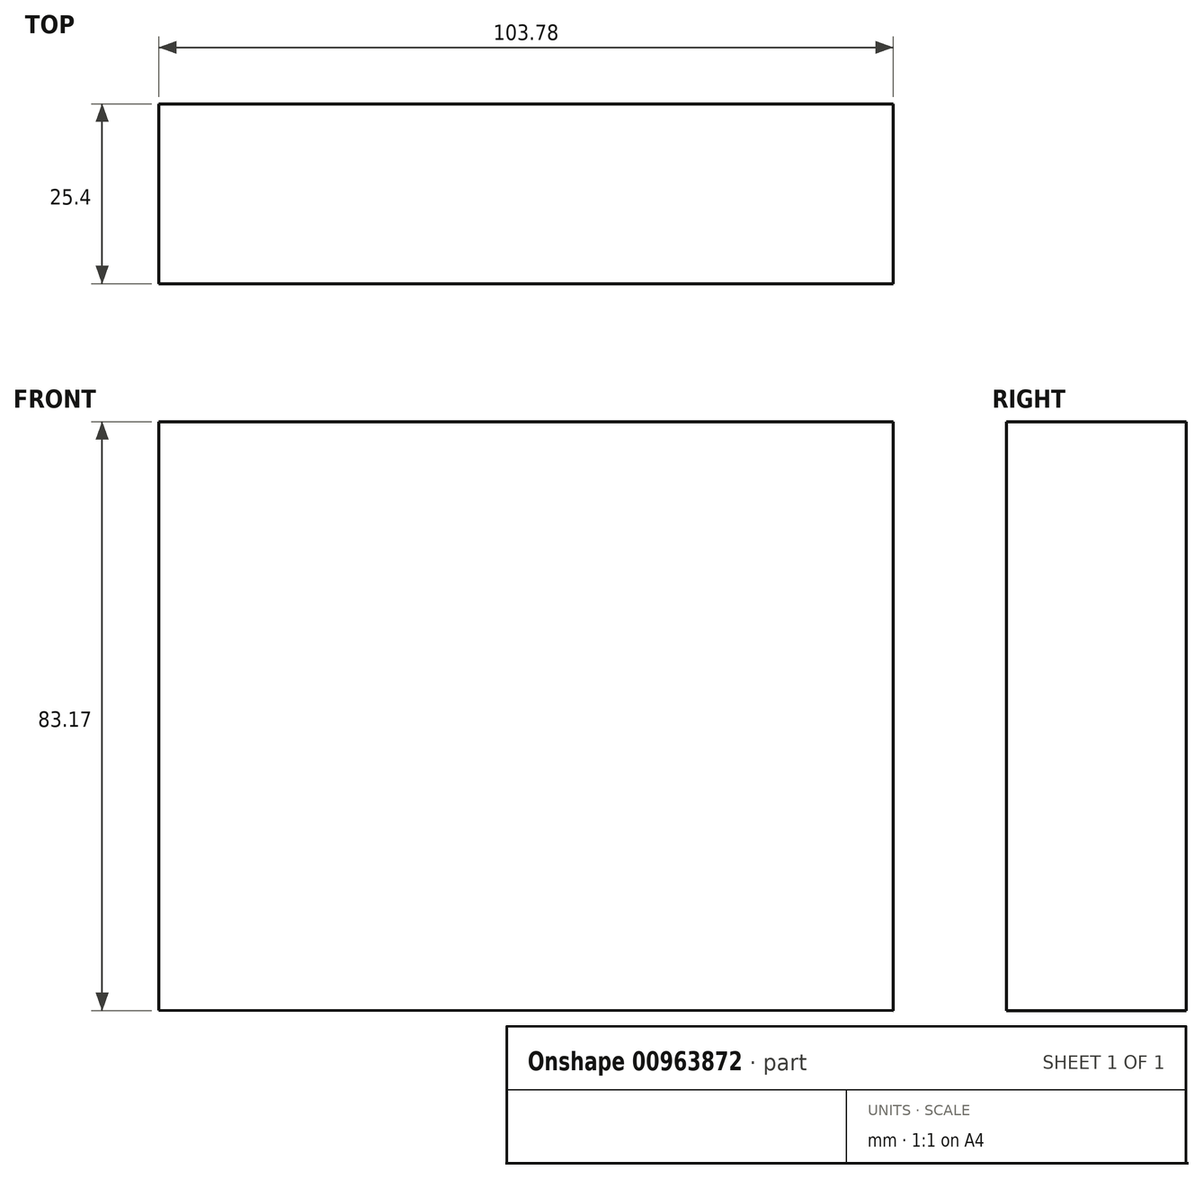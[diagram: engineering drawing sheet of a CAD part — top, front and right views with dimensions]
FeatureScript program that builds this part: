
annotation { "Feature Type Name" : "Feature", "Feature Type Description" : "" }
export const myFeature = defineFeature(function(context is Context, id is Id, definition is map)
    precondition{}
    {
        {
            var Q0;
            Q0=qCreatedBy(makeId("Front.planeOp"),FACE);
            var sketch = newSketch(context, id + "F0", { "sketchPlane" : qUnion([Q0])});
            skLineSegment(sketch, "E0", {"start": v(-44.93, 44.37) * mm, "end": v(58.85, 44.37) * mm});
            skLineSegment(sketch, "E1", {"start": v(58.85, 44.37) * mm, "end": v(58.85, -38.8) * mm});
            skLineSegment(sketch, "E2", {"start": v(58.85, -38.8) * mm, "end": v(-44.93, -38.74) * mm});
            skLineSegment(sketch, "E3", {"start": v(-44.93, 44.37) * mm, "end": v(-44.93, -38.74) * mm});
            skSolve(sketch);
        }
        {
            var Q0;
            Q0=makeQuery(id+"F0.imprint","IMPRINT",FACE,{"disambiguationData":[TD([[makeQuery(id+"F0.imprint","IMPRINT",EDGE,{"derivedFrom":sQuery(id+"F0.wireOp",EDGE,"E0")}),-1.0]])]});
            extrude(context, id + "F1", {"entities" : qUnion([Q0]), "endBound" : BoundingType.SYMMETRIC, "depth" : 25.4 * mm, "offsetDistance" : 25.4 * mm});
        }
    });
